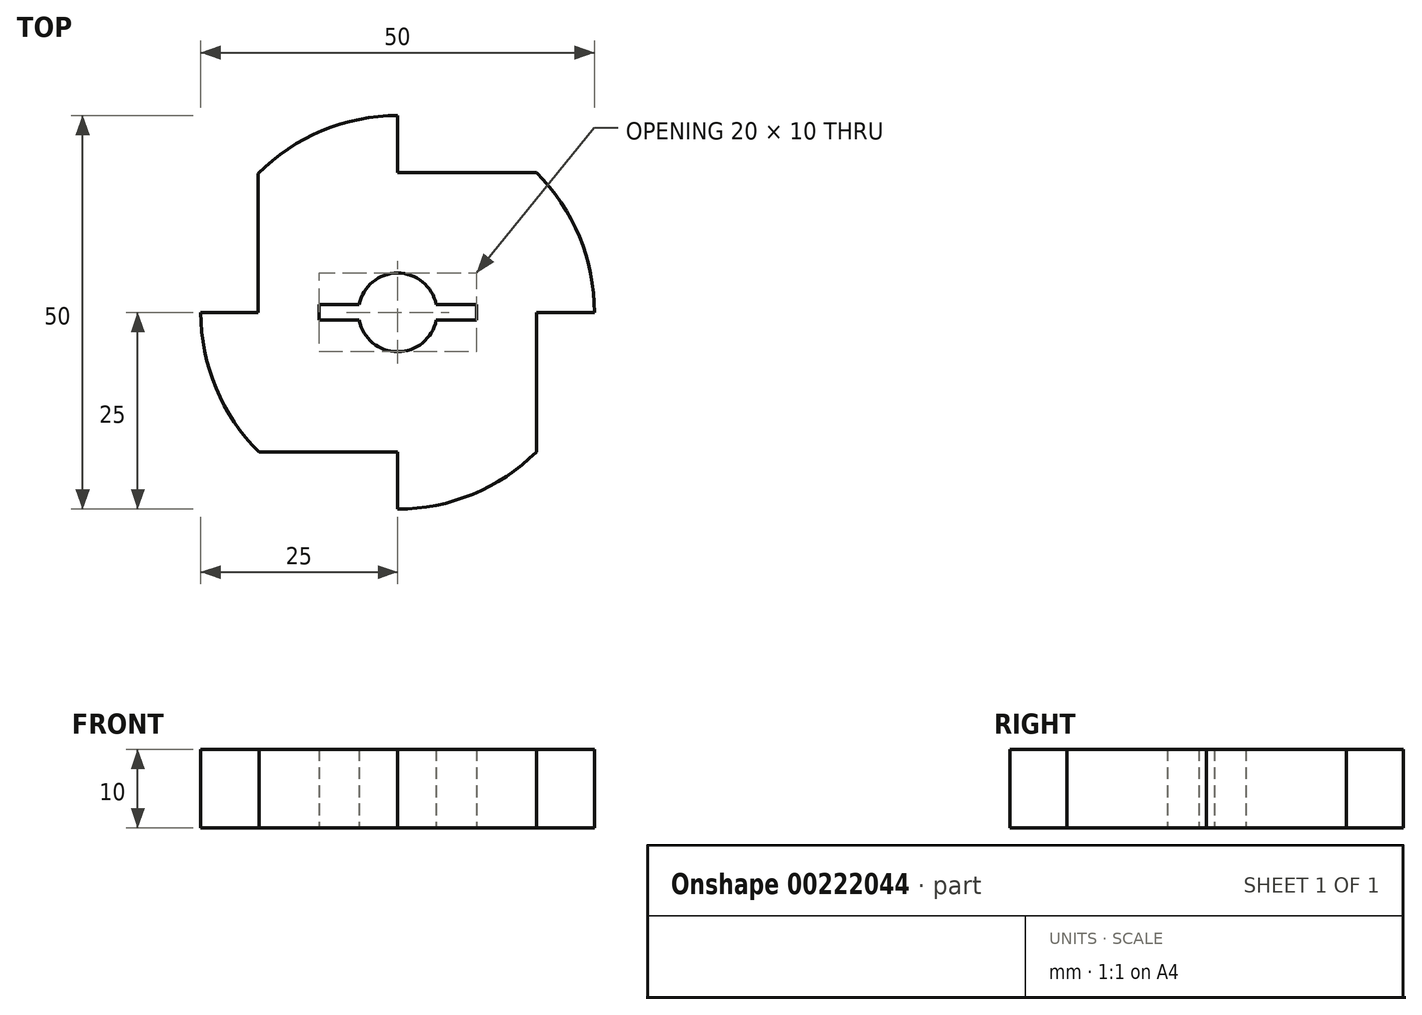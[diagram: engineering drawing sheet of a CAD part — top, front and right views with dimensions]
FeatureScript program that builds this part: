
annotation { "Feature Type Name" : "Feature", "Feature Type Description" : "" }
export const myFeature = defineFeature(function(context is Context, id is Id, definition is map)
    precondition{}
    {
        {
            var Q0;
            Q0=qCreatedBy(makeId("Top.planeOp"),FACE);
            var sketch = newSketch(context, id + "F0", { "sketchPlane" : qUnion([Q0])});
            skArc(sketch, "E0", {"start": v(0, 25) * mm, "mid": v(-9.6, 23.08) * mm, "end": v(-17.74, 17.61) * mm});
            skArc(sketch, "E1", {"start": v(-4.9, -1) * mm, "mid": v(0, -5) * mm, "end": v(4.9, -1) * mm});
            skLineSegment(sketch, "E2", {"start": v(0, 0) * mm, "end": v(10, 0) * mm, "construction": true});
            skLineSegment(sketch, "E3", {"start": v(0, 0) * mm, "end": v(-10, 0) * mm, "construction": true});
            skLineSegment(sketch, "E4", {"start": v(-10, 0) * mm, "end": v(-10, 1) * mm, "construction": true});
            skLineSegment(sketch, "E5", {"start": v(10, 0) * mm, "end": v(10, 1) * mm, "construction": true});
            skLineSegment(sketch, "E6", {"start": v(-10, 1) * mm, "end": v(-4.9, 1) * mm});
            skLineSegment(sketch, "E7.0", {"start": v(-10, -1) * mm, "end": v(-4.9, -1) * mm});
            skArc(sketch, "E8.trimOffspring", {"start": v(4.9, 1) * mm, "mid": v(0, 5) * mm, "end": v(-4.9, 1) * mm});
            skLineSegment(sketch, "E9", {"start": v(-10, 1) * mm, "end": v(-10, -1) * mm});
            skLineSegment(sketch, "E10", {"start": v(10, 1) * mm, "end": v(10, -1) * mm});
            skLineSegment(sketch, "E11.trimOffspring", {"start": v(4.9, 1) * mm, "end": v(10, 1) * mm});
            skLineSegment(sketch, "E12.trimOffspring", {"start": v(4.9, -1) * mm, "end": v(10, -1) * mm});
            skLineSegment(sketch, "E13", {"start": v(0, 0) * mm, "end": v(17.61, 17.74) * mm, "construction": true});
            skLineSegment(sketch, "E14", {"start": v(0, 0) * mm, "end": v(-17.74, 17.61) * mm, "construction": true});
            skLineSegment(sketch, "E15", {"start": v(0, 0) * mm, "end": v(-17.61, -17.74) * mm, "construction": true});
            skLineSegment(sketch, "E16", {"start": v(0, 0) * mm, "end": v(17.61, -17.74) * mm, "construction": true});
            skLineSegment(sketch, "E17", {"start": v(17.61, 17.74) * mm, "end": v(0, 17.74) * mm});
            skLineSegment(sketch, "E18", {"start": v(0, 25) * mm, "end": v(0, 17.74) * mm});
            skLineSegment(sketch, "E19", {"start": v(17.61, -17.74) * mm, "end": v(17.61, 0) * mm});
            skLineSegment(sketch, "E20", {"start": v(17.61, 0) * mm, "end": v(25, 0) * mm});
            skLineSegment(sketch, "E21", {"start": v(-17.61, -17.74) * mm, "end": v(0, -17.74) * mm});
            skLineSegment(sketch, "E22", {"start": v(0, -17.74) * mm, "end": v(0, -25) * mm});
            skLineSegment(sketch, "E23", {"start": v(-17.74, 17.61) * mm, "end": v(-17.74, 0) * mm});
            skLineSegment(sketch, "E24", {"start": v(-17.74, 0) * mm, "end": v(-25, 0) * mm});
            skArc(sketch, "E25.trimOffspring", {"start": v(-25, 0) * mm, "mid": v(-23.08, -9.6) * mm, "end": v(-17.61, -17.74) * mm});
            skArc(sketch, "E26.trimOffspring", {"start": v(25, 0) * mm, "mid": v(23.08, 9.6) * mm, "end": v(17.61, 17.74) * mm});
            skArc(sketch, "E27.trimOffspring", {"start": v(0, -25) * mm, "mid": v(9.53, -23.11) * mm, "end": v(17.61, -17.74) * mm});
            skSolve(sketch);
        }
        {
            var Q0;
            Q0 = qSketchRegion(id + "F0", true);
            extrude(context, id + "F1", {"entities" : qUnion([Q0]), "endBound" : BoundingType.SYMMETRIC, "depth" : 10 * mm});
        }
    });
